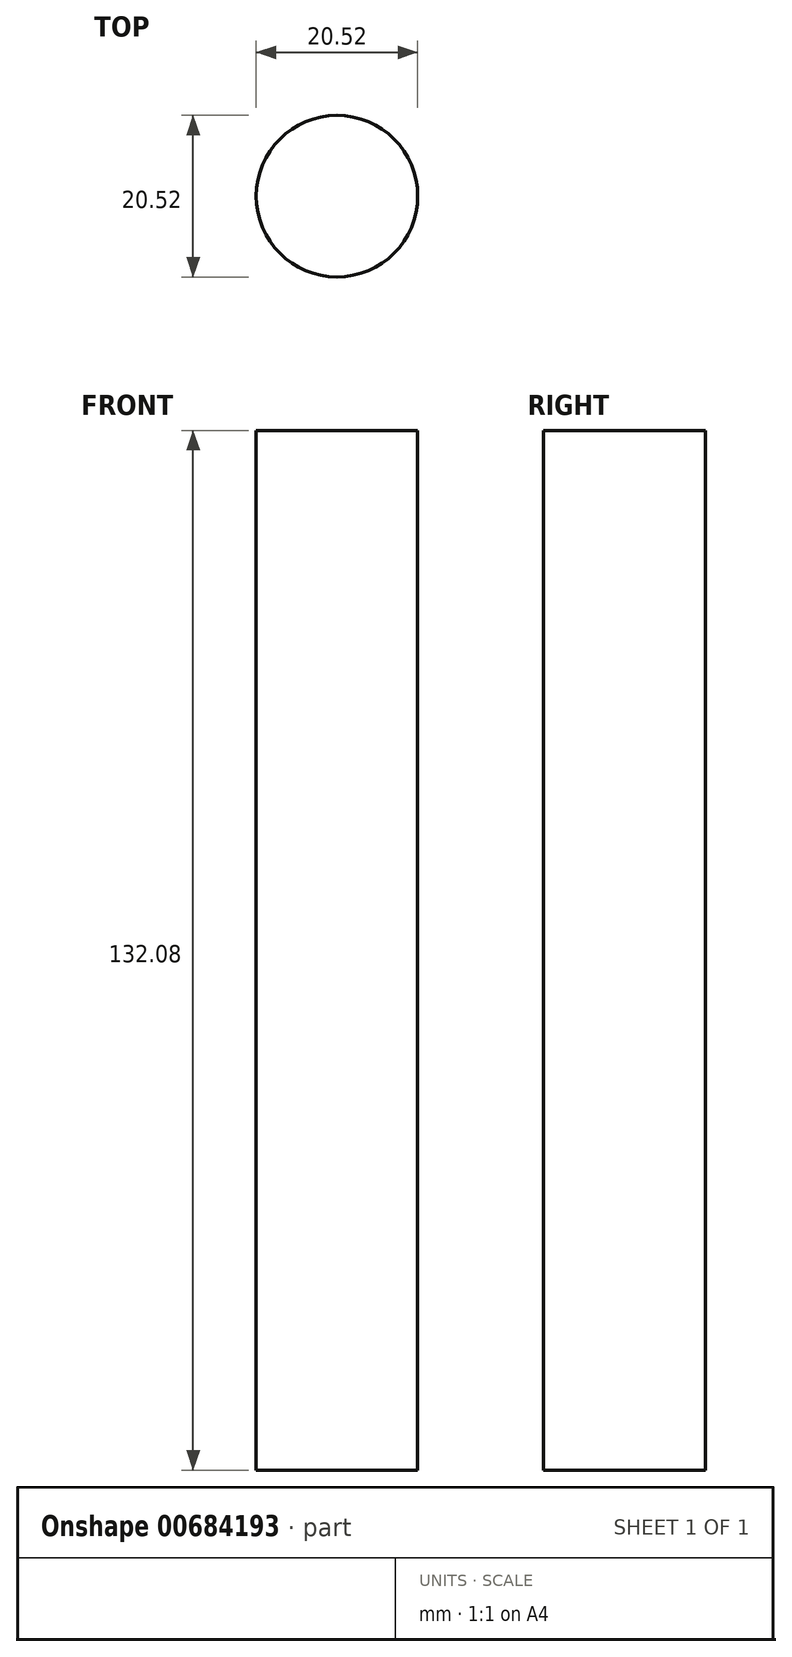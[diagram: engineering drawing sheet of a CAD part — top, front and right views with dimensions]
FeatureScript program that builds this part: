
annotation { "Feature Type Name" : "Feature", "Feature Type Description" : "" }
export const myFeature = defineFeature(function(context is Context, id is Id, definition is map)
    precondition{}
    {
        {
            var Q0;
            Q0=qCreatedBy(makeId("Front.planeOp"),FACE);
            var sketch = newSketch(context, id + "F0", { "sketchPlane" : qUnion([Q0])});
            skLineSegment(sketch, "E0.bottom", {"start": v(28.04, 20.89) * mm, "end": v(-27.68, 20.89) * mm});
            skLineSegment(sketch, "E0.top", {"start": v(28.04, -5.15) * mm, "end": v(-27.68, -5.15) * mm});
            skLineSegment(sketch, "E0.left", {"start": v(28.04, 20.89) * mm, "end": v(28.04, -5.15) * mm});
            skLineSegment(sketch, "E0.right", {"start": v(-27.68, 20.89) * mm, "end": v(-27.68, -5.15) * mm});
            skLineSegment(sketch, "E1", {"start": v(28.04, 20.89) * mm, "end": v(36.47, 27.5) * mm});
            skLineSegment(sketch, "E2", {"start": v(36.47, 27.5) * mm, "end": v(42.83, 10.95) * mm});
            skLineSegment(sketch, "E3", {"start": v(42.83, 10.95) * mm, "end": v(91.73, 81.29) * mm});
            skLineSegment(sketch, "E4", {"start": v(91.73, 81.29) * mm, "end": v(43.98, 34.94) * mm});
            skLineSegment(sketch, "E5", {"start": v(43.98, 34.94) * mm, "end": v(42.1, 52.18) * mm});
            skLineSegment(sketch, "E6", {"start": v(42.1, 52.18) * mm, "end": v(16.43, 20.89) * mm});
            skLineSegment(sketch, "E7", {"start": v(16.43, 20.89) * mm, "end": v(28.04, 20.89) * mm});
            skLineSegment(sketch, "E8", {"start": v(-27.68, 20.89) * mm, "end": v(-36.36, 27.5) * mm});
            skLineSegment(sketch, "E9", {"start": v(-36.36, 27.5) * mm, "end": v(-42.87, 10.95) * mm});
            skLineSegment(sketch, "E10", {"start": v(-42.87, 10.95) * mm, "end": v(-91.86, 81.29) * mm});
            skLineSegment(sketch, "E11", {"start": v(-91.86, 81.29) * mm, "end": v(-44, 34.94) * mm});
            skLineSegment(sketch, "E12", {"start": v(-44, 34.94) * mm, "end": v(-42.14, 52.1) * mm});
            skLineSegment(sketch, "E13", {"start": v(-42.14, 52.1) * mm, "end": v(-16.35, 20.89) * mm});
            skLineSegment(sketch, "E14", {"start": v(-16.35, 20.89) * mm, "end": v(-27.68, 20.89) * mm});
            skSolve(sketch);
        }
        {
            var Q0;
            Q0=makeQuery(id+"F0.imprint","IMPRINT",FACE,{"disambiguationData":[TD([[makeQuery(id+"F0.imprint","IMPRINT",EDGE,{"derivedFrom":sQuery(id+"F0.wireOp",EDGE,"E0.bottom")}),1.0]])]});
            var Q1;
            Q1=makeQuery(id+"F0.imprint","IMPRINT",FACE,{"disambiguationData":[TD([[makeQuery(id+"F0.imprint","IMPRINT",EDGE,{"derivedFrom":sQuery(id+"F0.wireOp",EDGE,"E1")}),1.0]])]});
            var Q2;
            Q2=makeQuery(id+"F0.imprint","IMPRINT",FACE,{"disambiguationData":[TD([[makeQuery(id+"F0.imprint","IMPRINT",EDGE,{"derivedFrom":sQuery(id+"F0.wireOp",EDGE,"E8")}),-1.0]])]});
            extrude(context, id + "F1", {"entities" : qUnion([Q0, Q1, Q2]), "depth" : 12.7 * mm, "offsetDistance" : 25.4 * mm});
        }
        {
            var Q0;
            Q0=makeQuery(id+"F1.opExtrude","CAP_FACE",FACE,{"disambiguationData":[OSD([sQuery(id+"F0.wireOp",EDGE,"E0.bottom"),sQuery(id+"F0.wireOp",EDGE,"E0.top"),sQuery(id+"F0.wireOp",EDGE,"E0.left"),sQuery(id+"F0.wireOp",EDGE,"E0.right"),sQuery(id+"F0.wireOp",EDGE,"E1"),sQuery(id+"F0.wireOp",EDGE,"E2"),sQuery(id+"F0.wireOp",EDGE,"E3"),sQuery(id+"F0.wireOp",EDGE,"E4"),sQuery(id+"F0.wireOp",EDGE,"E5"),sQuery(id+"F0.wireOp",EDGE,"E6"),sQuery(id+"F0.wireOp",EDGE,"E8"),sQuery(id+"F0.wireOp",EDGE,"E9"),sQuery(id+"F0.wireOp",EDGE,"E10"),sQuery(id+"F0.wireOp",EDGE,"E11"),sQuery(id+"F0.wireOp",EDGE,"E12"),sQuery(id+"F0.wireOp",EDGE,"E13")])],"isStart":true});
            extrude(context, id + "F2", {"entities" : qUnion([Q0]), "operationType" : NewBodyOperationType.ADD, "depth" : 12.7 * mm, "offsetDistance" : 25.4 * mm});
        }
        {
            var Q0;
            {var subQ0=sQuery(id+"F0.wireOp",EDGE,"E0.top");Q0=makeQuery(id+"F2.boolean.opBoolean","MERGE",FACE,{"derivedFrom":[makeQuery(id+"F1.opExtrude","SWEPT_FACE",FACE,{"disambiguationData":[OSD([subQ0])]}),makeQuery(id+"F2.opExtrude","SWEPT_FACE",FACE,{"disambiguationData":[OSD([subQ0])]})]});}
            var sketch = newSketch(context, id + "F3", { "sketchPlane" : qUnion([Q0])});
            skCircle(sketch, "E15", {"center": v(0, 0) * mm, "radius": 10.26 * mm});
            skSolve(sketch);
        }
        {
            var Q0;
            Q0=makeQuery(id+"F3.imprint","IMPRINT",FACE,{"disambiguationData":[TD([[makeQuery(id+"F3.imprint","IMPRINT",EDGE,{"derivedFrom":sQuery(id+"F3.wireOp",EDGE,"E15")}),1.0]])]});
            extrude(context, id + "F4", {"entities" : qUnion([Q0]), "operationType" : NewBodyOperationType.ADD, "depth" : 127 * mm, "offsetDistance" : 25.4 * mm});
        }
        {
            var Q0;
            Q0=makeQuery(id+"F4.opExtrude","CAP_FACE",FACE,{"disambiguationData":[OSD([sQuery(id+"F3.wireOp",EDGE,"E15")])],"isStart":false});
            extrude(context, id + "F5", {"entities" : qUnion([Q0]), "operationType" : NewBodyOperationType.REMOVE, "oppositeDirection" : true, "depth" : 25.4 * mm, "offsetDistance" : 25.4 * mm});
        }
        {
            var Q0;
            Q0=makeQuery(id+"F5.boolean.opBoolean","COPY",FACE,{"derivedFrom":makeQuery(id+"F5.opExtrude","CAP_FACE",FACE,{"disambiguationData":[OSD([sQuery(id+"F3.wireOp",EDGE,"E15")])],"isStart":false})});
            extrude(context, id + "F6", {"entities" : qUnion([Q0]), "operationType" : NewBodyOperationType.ADD, "depth" : 12.7 * mm, "offsetDistance" : 25.4 * mm});
        }
        {
            var Q0;
            Q0=makeQuery(id+"F6.opExtrude","CAP_FACE",FACE,{"disambiguationData":[OSD([sQuery(id+"F3.wireOp",EDGE,"E15")])],"isStart":false});
            extrude(context, id + "F7", {"entities" : qUnion([Q0]), "operationType" : NewBodyOperationType.REMOVE, "oppositeDirection" : true, "depth" : 2.54 * mm, "offsetDistance" : 25.4 * mm});
        }
        {
            var Q0;
            Q0=makeQuery(id+"F1.opExtrude","CAP_FACE",FACE,{"disambiguationData":[OSD([sQuery(id+"F0.wireOp",EDGE,"E0.bottom"),sQuery(id+"F0.wireOp",EDGE,"E0.top"),sQuery(id+"F0.wireOp",EDGE,"E0.left"),sQuery(id+"F0.wireOp",EDGE,"E0.right"),sQuery(id+"F0.wireOp",EDGE,"E1"),sQuery(id+"F0.wireOp",EDGE,"E2"),sQuery(id+"F0.wireOp",EDGE,"E3"),sQuery(id+"F0.wireOp",EDGE,"E4"),sQuery(id+"F0.wireOp",EDGE,"E5"),sQuery(id+"F0.wireOp",EDGE,"E6"),sQuery(id+"F0.wireOp",EDGE,"E8"),sQuery(id+"F0.wireOp",EDGE,"E9"),sQuery(id+"F0.wireOp",EDGE,"E10"),sQuery(id+"F0.wireOp",EDGE,"E11"),sQuery(id+"F0.wireOp",EDGE,"E12"),sQuery(id+"F0.wireOp",EDGE,"E13")])],"isStart":false});
            extrude(context, id + "F8", {"entities" : qUnion([Q0]), "operationType" : NewBodyOperationType.REMOVE, "oppositeDirection" : true, "depth" : 25.4 * mm, "offsetDistance" : 25.4 * mm});
        }
        {
            var Q0;
            Q0=makeQuery(id+"F8.boolean.opBoolean","COPY",FACE,{"derivedFrom":makeQuery(id+"F8.opExtrude","SWEPT_FACE",FACE,{"disambiguationData":[OSD([sQuery(id+"F0.wireOp",EDGE,"E0.top")])]})});
            extrude(context, id + "F9", {"entities" : qUnion([Q0]), "operationType" : NewBodyOperationType.ADD, "depth" : 25.4 * mm, "offsetDistance" : 25.4 * mm});
        }
        {
            var Q0;
            Q0=makeQuery(id+"F9.opExtrude","CAP_FACE",FACE,{"disambiguationData":[OSD([sQuery(id+"F0.wireOp",EDGE,"E0.top")])],"isStart":false});
            extrude(context, id + "F10", {"entities" : qUnion([Q0]), "operationType" : NewBodyOperationType.REMOVE, "oppositeDirection" : true, "depth" : 5.08 * mm, "offsetDistance" : 25.4 * mm});
        }
    });
